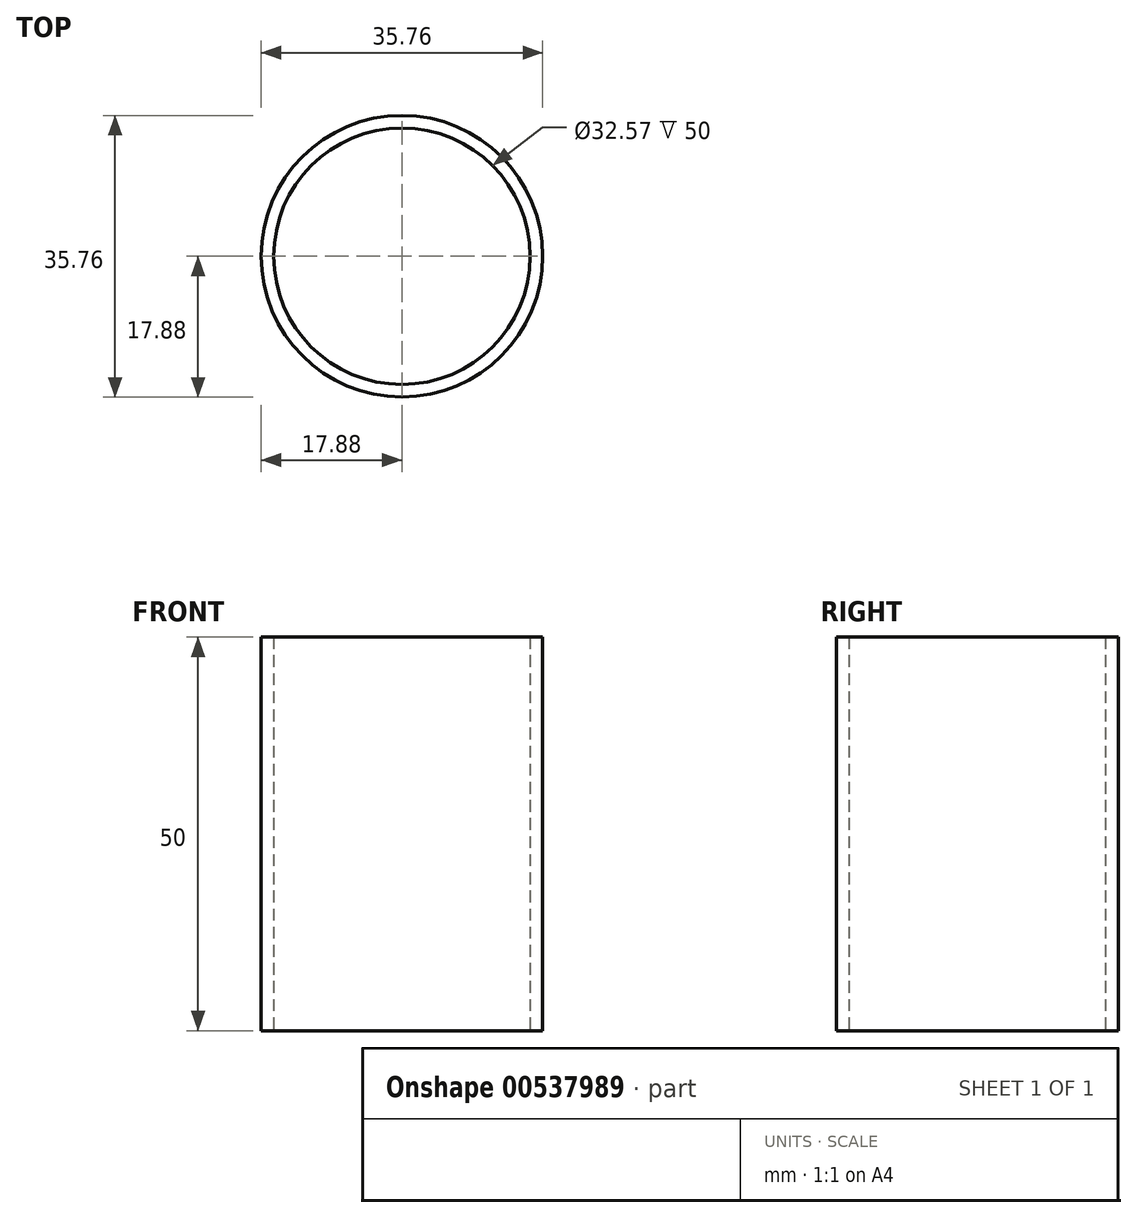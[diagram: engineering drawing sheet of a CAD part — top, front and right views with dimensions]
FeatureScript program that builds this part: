
annotation { "Feature Type Name" : "Feature", "Feature Type Description" : "" }
export const myFeature = defineFeature(function(context is Context, id is Id, definition is map)
    precondition{}
    {
        {
            var Q0;
            Q0=qCreatedBy(makeId("Top.planeOp"),FACE);
            var sketch = newSketch(context, id + "F0", { "sketchPlane" : qUnion([Q0])});
            skCircle(sketch, "E0", {"center": v(0, 0) * mm, "radius": 17.88 * mm});
            skCircle(sketch, "E1", {"center": v(0, 0) * mm, "radius": 16.28 * mm});
            skSolve(sketch);
        }
        {
            var Q0;
            Q0=makeQuery(id+"F0.imprint","IMPRINT",FACE,{"disambiguationData":[TD([[makeQuery(id+"F0.imprint","IMPRINT",EDGE,{"derivedFrom":sQuery(id+"F0.wireOp",EDGE,"E0")}),1.0]])]});
            extrude(context, id + "F1", {"entities" : qUnion([Q0]), "depth" : 50 * mm, "offsetDistance" : 25 * mm});
        }
    });
